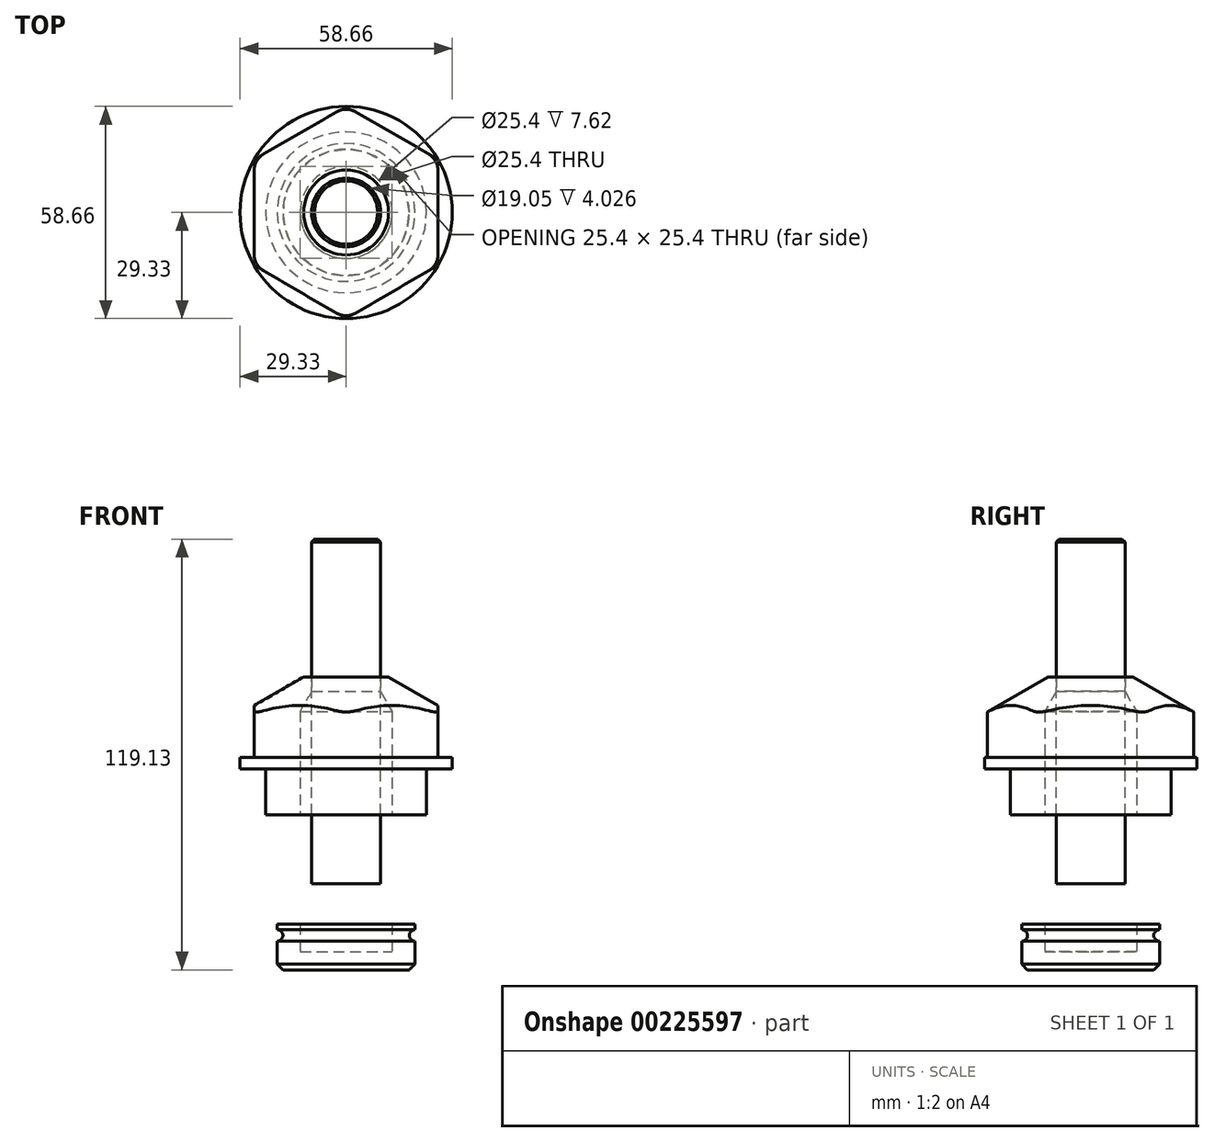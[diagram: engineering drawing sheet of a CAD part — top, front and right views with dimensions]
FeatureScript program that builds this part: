
annotation { "Feature Type Name" : "Feature", "Feature Type Description" : "" }
export const myFeature = defineFeature(function(context is Context, id is Id, definition is map)
    precondition{}
    {
        {
            var Q0;
            Q0=qCreatedBy(makeId("Top.planeOp"),FACE);
            var sketch = newSketch(context, id + "F0", { "sketchPlane" : qUnion([Q0])});
            skCircle(sketch, "E0", {"center": v(0, 0) * mm, "radius": 29.33 * mm});
            skLineSegment(sketch, "E1", {"start": v(0, 29.33) * mm, "end": v(0, -29.33) * mm, "construction": true});
            skLineSegment(sketch, "E2", {"start": v(-25.4, 14.66) * mm, "end": v(25.4, -14.66) * mm, "construction": true});
            skLineSegment(sketch, "E3", {"start": v(-25.4, -14.66) * mm, "end": v(25.4, 14.66) * mm, "construction": true});
            skLineSegment(sketch, "E4", {"start": v(-25.4, 14.66) * mm, "end": v(0, 29.33) * mm});
            skLineSegment(sketch, "E5", {"start": v(0, 29.33) * mm, "end": v(25.4, 14.66) * mm});
            skLineSegment(sketch, "E6", {"start": v(25.4, 14.66) * mm, "end": v(25.4, -14.66) * mm});
            skLineSegment(sketch, "E7", {"start": v(25.4, -14.66) * mm, "end": v(0, -29.33) * mm});
            skLineSegment(sketch, "E8", {"start": v(0, -29.33) * mm, "end": v(-25.4, -14.66) * mm});
            skLineSegment(sketch, "E9", {"start": v(-25.4, -14.66) * mm, "end": v(-25.4, 14.66) * mm});
            skCircle(sketch, "E10", {"center": v(0, 0) * mm, "radius": 7.94 * mm});
            skSolve(sketch);
        }
        {
            var Q0;
            Q0=makeQuery(id+"F0.imprint","IMPRINT",FACE,{"disambiguationData":[TD([[makeQuery(id+"F0.imprint","IMPRINT",EDGE,{"derivedFrom":sQuery(id+"F0.wireOp",EDGE,"E10")}),1.0]])]});
            var Q1;
            Q1=makeQuery(id+"F0.imprint","IMPRINT",FACE,{"disambiguationData":[TD([[makeQuery(id+"F0.imprint","IMPRINT",EDGE,{"derivedFrom":sQuery(id+"F0.wireOp",EDGE,"E4")}),-1.0]])]});
            extrude(context, id + "F1", {"entities" : qUnion([Q0, Q1]), "depth" : 25.4 * mm});
        }
        {
            var Q0;
            {var subQ0=sQuery(id+"F0.wireOp",EDGE,"E8");Q0=makeQuery(id+"F0.imprint","IMPRINT",FACE,{"disambiguationData":[TD([[makeQuery(id+"F0.imprint","IMPRINT",EDGE,{"derivedFrom":subQ0}),1.0]])]});}
            var Q1;
            {var subQ0=sQuery(id+"F0.wireOp",EDGE,"E7");Q1=makeQuery(id+"F0.imprint","IMPRINT",FACE,{"disambiguationData":[TD([[makeQuery(id+"F0.imprint","IMPRINT",EDGE,{"derivedFrom":subQ0}),1.0]])]});}
            var Q2;
            {var subQ0=sQuery(id+"F0.wireOp",EDGE,"E6");Q2=makeQuery(id+"F0.imprint","IMPRINT",FACE,{"disambiguationData":[TD([[makeQuery(id+"F0.imprint","IMPRINT",EDGE,{"derivedFrom":subQ0}),1.0]])]});}
            var Q3;
            Q3=makeQuery(id+"F0.imprint","IMPRINT",FACE,{"disambiguationData":[TD([[makeQuery(id+"F0.imprint","IMPRINT",EDGE,{"derivedFrom":sQuery(id+"F0.wireOp",EDGE,"E4")}),-1.0]])]});
            var Q4;
            {var subQ0=sQuery(id+"F0.wireOp",EDGE,"E5");Q4=makeQuery(id+"F0.imprint","IMPRINT",FACE,{"disambiguationData":[TD([[makeQuery(id+"F0.imprint","IMPRINT",EDGE,{"derivedFrom":subQ0}),1.0]])]});}
            var Q5;
            {var subQ0=sQuery(id+"F0.wireOp",EDGE,"E4");Q5=makeQuery(id+"F0.imprint","IMPRINT",FACE,{"disambiguationData":[TD([[makeQuery(id+"F0.imprint","IMPRINT",EDGE,{"derivedFrom":subQ0}),1.0]])]});}
            var Q6;
            {var subQ0=sQuery(id+"F0.wireOp",EDGE,"E9");Q6=makeQuery(id+"F0.imprint","IMPRINT",FACE,{"disambiguationData":[TD([[makeQuery(id+"F0.imprint","IMPRINT",EDGE,{"derivedFrom":subQ0}),1.0]])]});}
            extrude(context, id + "F2", {"entities" : qUnion([Q0, Q1, Q2, Q3, Q4, Q5, Q6]), "operationType" : NewBodyOperationType.ADD, "depth" : 3.17 * mm});
        }
        {
            var Q0;
            Q0=makeQuery(id+"F1.opExtrude","SWEPT_EDGE",EDGE,{"disambiguationData":[OSD([sQuery(id+"F0.wireOp",EDGE,"E0"),sQuery(id+"F0.wireOp",EDGE,"E7"),sQuery(id+"F0.wireOp",EDGE,"E8")])]});
            var Q1;
            Q1=makeQuery(id+"F1.opExtrude","SWEPT_EDGE",EDGE,{"disambiguationData":[OSD([sQuery(id+"F0.wireOp",EDGE,"E0"),sQuery(id+"F0.wireOp",EDGE,"E6"),sQuery(id+"F0.wireOp",EDGE,"E7")])]});
            var Q2;
            Q2=makeQuery(id+"F1.opExtrude","SWEPT_EDGE",EDGE,{"disambiguationData":[OSD([sQuery(id+"F0.wireOp",EDGE,"E0"),sQuery(id+"F0.wireOp",EDGE,"E5"),sQuery(id+"F0.wireOp",EDGE,"E6")])]});
            var Q3;
            Q3=makeQuery(id+"F1.opExtrude","SWEPT_EDGE",EDGE,{"disambiguationData":[OSD([sQuery(id+"F0.wireOp",EDGE,"E0"),sQuery(id+"F0.wireOp",EDGE,"E4"),sQuery(id+"F0.wireOp",EDGE,"E5")])]});
            var Q4;
            Q4=makeQuery(id+"F1.opExtrude","SWEPT_EDGE",EDGE,{"disambiguationData":[OSD([sQuery(id+"F0.wireOp",EDGE,"E0"),sQuery(id+"F0.wireOp",EDGE,"E4"),sQuery(id+"F0.wireOp",EDGE,"E9")])]});
            var Q5;
            Q5=makeQuery(id+"F1.opExtrude","SWEPT_EDGE",EDGE,{"disambiguationData":[OSD([sQuery(id+"F0.wireOp",EDGE,"E0"),sQuery(id+"F0.wireOp",EDGE,"E8"),sQuery(id+"F0.wireOp",EDGE,"E9")])]});
            fillet(context, id + "F3", {"entities" : qUnion([Q0, Q1, Q2, Q3, Q4, Q5]), "radius" : 5.08 * mm, "tangentPropagation" : true, "allowEdgeOverflow" : false});
        }
        {
            var Q0;
            Q0=qCreatedBy(makeId("Right.planeOp"),FACE);
            var sketch = newSketch(context, id + "F4", { "sketchPlane" : qUnion([Q0])});
            skLineSegment(sketch, "E11", {"start": v(0, 52) * mm, "end": v(0, 0) * mm, "construction": true});
            skLineSegment(sketch, "E12", {"start": v(11.73, 25.4) * mm, "end": v(35.4, 11.74) * mm});
            skLineSegment(sketch, "E13", {"start": v(35.4, 11.74) * mm, "end": v(35.4, 25.4) * mm});
            skLineSegment(sketch, "E14", {"start": v(35.4, 25.4) * mm, "end": v(11.73, 25.4) * mm});
            skLineSegment(sketch, "E15.0", {"start": v(11.73, 25.4) * mm, "end": v(-11.73, 25.4) * mm});
            skLineSegment(sketch, "E16.bottom", {"start": v(0, 0) * mm, "end": v(22.23, 0) * mm});
            skLineSegment(sketch, "E16.top", {"start": v(0, -12.7) * mm, "end": v(22.23, -12.7) * mm});
            skLineSegment(sketch, "E16.left", {"start": v(0, 0) * mm, "end": v(0, -12.7) * mm});
            skLineSegment(sketch, "E16.right", {"start": v(22.23, 0) * mm, "end": v(22.23, -12.7) * mm});
            skLineSegment(sketch, "E17.bottom", {"start": v(0, -12.7) * mm, "end": v(19.05, -12.7) * mm});
            skLineSegment(sketch, "E17.top", {"start": v(0, -27.69) * mm, "end": v(19.05, -27.69) * mm});
            skLineSegment(sketch, "E17.left", {"start": v(0, -12.7) * mm, "end": v(0, -27.69) * mm});
            skLineSegment(sketch, "E17.right", {"start": v(19.05, -12.7) * mm, "end": v(19.05, -27.69) * mm});
            skLineSegment(sketch, "E18.bottom", {"start": v(17.78, -27.69) * mm, "end": v(0, -27.69) * mm});
            skLineSegment(sketch, "E18.top", {"start": v(17.78, -42.93) * mm, "end": v(0, -42.93) * mm});
            skLineSegment(sketch, "E18.left", {"start": v(17.78, -27.69) * mm, "end": v(17.78, -42.93) * mm});
            skLineSegment(sketch, "E18.right", {"start": v(0, -27.69) * mm, "end": v(0, -42.93) * mm});
            skLineSegment(sketch, "E19.bottom", {"start": v(0, -42.93) * mm, "end": v(19.05, -42.93) * mm});
            skLineSegment(sketch, "E19.top", {"start": v(0, -55.63) * mm, "end": v(19.05, -55.63) * mm});
            skLineSegment(sketch, "E19.left", {"start": v(0, -42.93) * mm, "end": v(0, -55.63) * mm});
            skLineSegment(sketch, "E19.right", {"start": v(19.05, -42.93) * mm, "end": v(19.05, -55.63) * mm});
            skCircle(sketch, "E20", {"center": v(19.05, -24.51) * mm, "radius": 1.59 * mm});
            skCircle(sketch, "E21", {"center": v(19.05, -46.1) * mm, "radius": 1.59 * mm});
            skCircle(sketch, "E22", {"center": v(0, -17.46) * mm, "radius": 3.18 * mm});
            skCircle(sketch, "E23", {"center": v(0, -35.3) * mm, "radius": 3.18 * mm});
            skSolve(sketch);
        }
        {
            var Q0;
            Q0=makeQuery(id+"F4.imprint","IMPRINT",FACE,{"disambiguationData":[TD([[makeQuery(id+"F4.imprint","IMPRINT",EDGE,{"derivedFrom":sQuery(id+"F4.wireOp",EDGE,"E12")}),1.0]])]});
            var Q1;
            Q1=sQuery(id+"F4.wireOp",EDGE,"E11");
            revolve(context, id + "F5", {"operationType" : NewBodyOperationType.REMOVE, "entities" : qUnion([Q0]), "axis" : qUnion([Q1]), "revolveType" : RevolveType.FULL, "oppositeDirection" : true});
        }
        {
            var Q0;
            {var subQ7=sQuery(id+"F4.wireOp",EDGE,"E18.bottom");Q0=makeQuery(id+"F4.imprint","IMPRINT",FACE,{"disambiguationData":[TD([[makeQuery(id+"F4.imprint","IMPRINT",EDGE,{"derivedFrom":subQ7}),1.0]])]});}
            var Q1;
            {var subQ10=sQuery(id+"F4.wireOp",EDGE,"E17.bottom");Q1=makeQuery(id+"F4.imprint","IMPRINT",FACE,{"disambiguationData":[TD([[makeQuery(id+"F4.imprint","IMPRINT",EDGE,{"derivedFrom":subQ10}),-1.0]])]});}
            var Q2;
            Q2=makeQuery(id+"F4.imprint","IMPRINT",FACE,{"disambiguationData":[TD([[makeQuery(id+"F4.imprint","IMPRINT",EDGE,{"derivedFrom":sQuery(id+"F4.wireOp",EDGE,"E16.bottom")}),-1.0]])]});
            var Q3;
            {var subQ4=sQuery(id+"F4.wireOp",EDGE,"E19.top");Q3=makeQuery(id+"F4.imprint","IMPRINT",FACE,{"disambiguationData":[TD([[makeQuery(id+"F4.imprint","IMPRINT",EDGE,{"derivedFrom":subQ4}),1.0]])]});}
            var Q4;
            Q4=sQuery(id+"F4.wireOp",EDGE,"E11");
            revolve(context, id + "F6", {"operationType" : NewBodyOperationType.ADD, "entities" : qUnion([Q0, Q1, Q2, Q3]), "axis" : qUnion([Q4]), "revolveType" : RevolveType.FULL});
        }
        {
            var Q0;
            Q0=makeQuery(id+"F6.opRevolve","SWEPT_EDGE",EDGE,{"disambiguationData":[OSD([sQuery(id+"F4.wireOp",EDGE,"E19.top"),sQuery(id+"F4.wireOp",EDGE,"E19.right")])]});
            chamfer(context, id + "F7", {"entities" : qUnion([Q0]), "width" : 1.59 * mm, "tangentPropagation" : true});
        }
        {
            var Q0;
            {var subQ0=sQuery(id+"F4.wireOp",EDGE,"E16.right");var subQ1=sQuery(id+"F4.wireOp",EDGE,"E20");var subQ3=makeQuery(id+"F4.imprint","INTERSECT",VERTEX,{"disambiguationData":[OD(0.0)],"derivedFrom":[subQ0,subQ1]});Q0=makeQuery(id+"F4.imprint","IMPRINT",FACE,{"disambiguationData":[TD([[makeQuery(id+"F4.imprint","SKETCH_ENTITY",EDGE,{"disambiguationData":[TD([[subQ3,-1.0]])],"sketchEntityId":"E16.right"}),1.0]])]});}
            var Q1;
            {var subQ0=sQuery(id+"F4.wireOp",EDGE,"E20");var subQ1=sQuery(id+"F4.wireOp",EDGE,"E17.right");var subQ3=makeQuery(id+"F4.imprint","INTERSECT",VERTEX,{"disambiguationData":[OD(0.0)],"derivedFrom":[subQ1,subQ0]});Q1=makeQuery(id+"F4.imprint","IMPRINT",FACE,{"disambiguationData":[TD([[makeQuery(id+"F4.imprint","IMPRINT",EDGE,{"disambiguationData":[TD([[subQ3,-1.0]])],"derivedFrom":subQ1}),-1.0]])]});}
            var Q2;
            {var subQ0=sQuery(id+"F4.wireOp",EDGE,"E20");var subQ1=sQuery(id+"F4.wireOp",EDGE,"E17.right");var subQ3=makeQuery(id+"F4.imprint","INTERSECT",VERTEX,{"disambiguationData":[OD(0.0)],"derivedFrom":[subQ1,subQ0]});Q2=makeQuery(id+"F4.imprint","IMPRINT",FACE,{"disambiguationData":[TD([[makeQuery(id+"F4.imprint","IMPRINT",EDGE,{"disambiguationData":[TD([[subQ3,-1.0]])],"derivedFrom":subQ1}),1.0]])]});}
            var Q3;
            Q3=sQuery(id+"F4.wireOp",EDGE,"E11");
            revolve(context, id + "F8", {"entities" : qUnion([Q0, Q1, Q2]), "axis" : qUnion([Q3]), "revolveType" : RevolveType.FULL});
        }
        {
            var Q0;
            {var subQ0=sQuery(id+"F4.wireOp",EDGE,"E22");var subQ1=sQuery(id+"F4.wireOp",EDGE,"E17.left");var subQ3=makeQuery(id+"F4.imprint","INTERSECT",VERTEX,{"disambiguationData":[OD(0.0)],"derivedFrom":[subQ1,subQ0]});Q0=makeQuery(id+"F4.imprint","IMPRINT",FACE,{"disambiguationData":[TD([[makeQuery(id+"F4.imprint","IMPRINT",EDGE,{"disambiguationData":[TD([[subQ3,-1.0]])],"derivedFrom":subQ1}),-1.0]])]});}
            var Q1;
            {var subQ0=sQuery(id+"F4.wireOp",EDGE,"E22");var subQ1=sQuery(id+"F4.wireOp",EDGE,"E17.left");var subQ3=makeQuery(id+"F4.imprint","INTERSECT",VERTEX,{"disambiguationData":[OD(0.0)],"derivedFrom":[subQ1,subQ0]});Q1=makeQuery(id+"F4.imprint","IMPRINT",FACE,{"disambiguationData":[TD([[makeQuery(id+"F4.imprint","IMPRINT",EDGE,{"disambiguationData":[TD([[subQ3,-1.0]])],"derivedFrom":subQ1}),1.0]])]});}
            var Q2;
            {var subQ0=sQuery(id+"F4.wireOp",EDGE,"E23");var subQ1=sQuery(id+"F4.wireOp",EDGE,"E18.right");var subQ3=makeQuery(id+"F4.imprint","INTERSECT",VERTEX,{"disambiguationData":[OD(0.0)],"derivedFrom":[subQ1,subQ0]});Q2=makeQuery(id+"F4.imprint","IMPRINT",FACE,{"disambiguationData":[TD([[makeQuery(id+"F4.imprint","IMPRINT",EDGE,{"disambiguationData":[TD([[subQ3,-1.0]])],"derivedFrom":subQ1}),-1.0]])]});}
            var Q3;
            {var subQ0=sQuery(id+"F4.wireOp",EDGE,"E23");var subQ1=sQuery(id+"F4.wireOp",EDGE,"E18.right");var subQ3=makeQuery(id+"F4.imprint","INTERSECT",VERTEX,{"disambiguationData":[OD(0.0)],"derivedFrom":[subQ1,subQ0]});Q3=makeQuery(id+"F4.imprint","IMPRINT",FACE,{"disambiguationData":[TD([[makeQuery(id+"F4.imprint","IMPRINT",EDGE,{"disambiguationData":[TD([[subQ3,-1.0]])],"derivedFrom":subQ1}),1.0]])]});}
            extrude(context, id + "F9", {"entities" : qUnion([Q0, Q1, Q2, Q3]), "operationType" : NewBodyOperationType.REMOVE, "endBound" : BoundingType.THROUGH_ALL, "depth" : 25.4 * mm});
        }
        {
            var Q0;
            Q0=qCreatedBy(makeId("Right.planeOp"),FACE);
            var sketch = newSketch(context, id + "F10", { "sketchPlane" : qUnion([Q0])});
            skLineSegment(sketch, "E24", {"start": v(0, 63.5) * mm, "end": v(0, -50.55) * mm});
            skLineSegment(sketch, "E25", {"start": v(0, -50.55) * mm, "end": v(12.7, -50.55) * mm});
            skLineSegment(sketch, "E26", {"start": v(12.7, -50.55) * mm, "end": v(12.7, 15.88) * mm});
            skLineSegment(sketch, "E27", {"start": v(12.7, 15.88) * mm, "end": v(0, 15.88) * mm});
            skLineSegment(sketch, "E28", {"start": v(9.53, -31.75) * mm, "end": v(9.53, 63.5) * mm});
            skLineSegment(sketch, "E29", {"start": v(9.52, 63.5) * mm, "end": v(0, 63.5) * mm});
            skLineSegment(sketch, "E30", {"start": v(9.53, 21.37) * mm, "end": v(12.7, 15.88) * mm});
            skLineSegment(sketch, "E31.rect.bottom", {"start": v(12.7, -38.1) * mm, "end": v(-12.7, -38.1) * mm});
            skLineSegment(sketch, "E31.rect.top", {"start": v(12.7, -31.75) * mm, "end": v(-12.7, -31.75) * mm});
            skLineSegment(sketch, "E31.rect.left", {"start": v(12.7, -38.1) * mm, "end": v(12.7, -31.75) * mm});
            skLineSegment(sketch, "E31.rect.right", {"start": v(-12.7, -38.1) * mm, "end": v(-12.7, -31.75) * mm});
            skPoint(sketch, "E31.rect.middle", {"position": v(0, -34.92) * mm});
            skSolve(sketch);
        }
        {
            var Q0;
            {var subQ0=sQuery(id+"F10.wireOp",EDGE,"E29");Q0=makeQuery(id+"F10.imprint","IMPRINT",FACE,{"disambiguationData":[TD([[makeQuery(id+"F10.imprint","IMPRINT",EDGE,{"derivedFrom":subQ0}),1.0]])]});}
            var Q1;
            {var subQ0=sQuery(id+"F10.wireOp",EDGE,"E30");Q1=makeQuery(id+"F10.imprint","IMPRINT",FACE,{"disambiguationData":[TD([[makeQuery(id+"F10.imprint","IMPRINT",EDGE,{"derivedFrom":subQ0}),-1.0]])]});}
            var Q2;
            {var subQ1=sQuery(id+"F10.wireOp",EDGE,"E24");var subQ5=sQuery(id+"F10.wireOp",EDGE,"E27");var subQ7=makeQuery(id+"F10.imprint","INTERSECT",VERTEX,{"derivedFrom":[subQ1,subQ5]});Q2=makeQuery(id+"F10.imprint","IMPRINT",FACE,{"disambiguationData":[TD([[makeQuery(id+"F10.imprint","IMPRINT",EDGE,{"disambiguationData":[TD([[subQ7,-1.0]])],"derivedFrom":subQ1}),1.0]])]});}
            var Q3;
            {var subQ0=sQuery(id+"F10.wireOp",EDGE,"E31.rect.top");var subQ3=sQuery(id+"F10.wireOp",EDGE,"E28");var subQ4=makeQuery(id+"F10.imprint","INTERSECT",VERTEX,{"derivedFrom":[subQ3,subQ0]});Q3=makeQuery(id+"F10.imprint","IMPRINT",FACE,{"disambiguationData":[TD([[makeQuery(id+"F10.imprint","IMPRINT",EDGE,{"disambiguationData":[TD([[subQ4,-1.0]])],"derivedFrom":subQ3}),-1.0]])]});}
            var Q4;
            {var subQ5=sQuery(id+"F10.wireOp",EDGE,"E25");Q4=makeQuery(id+"F10.imprint","IMPRINT",FACE,{"disambiguationData":[TD([[makeQuery(id+"F10.imprint","IMPRINT",EDGE,{"derivedFrom":subQ5}),1.0]])]});}
            var Q5;
            {var subQ0=sQuery(id+"F10.wireOp",EDGE,"E31.rect.left");Q5=makeQuery(id+"F10.imprint","IMPRINT",FACE,{"disambiguationData":[TD([[makeQuery(id+"F10.imprint","IMPRINT",EDGE,{"derivedFrom":subQ0}),1.0]])]});}
            var Q6;
            Q6=sQuery(id+"F10.wireOp",EDGE,"E24");
            revolve(context, id + "F11", {"operationType" : NewBodyOperationType.REMOVE, "entities" : qUnion([Q0, Q1, Q2, Q3, Q4, Q5]), "axis" : qUnion([Q6]), "revolveType" : RevolveType.FULL, "oppositeDirection" : true});
        }
        {
            var Q0;
            {var subQ0=sQuery(id+"F10.wireOp",EDGE,"E29");Q0=makeQuery(id+"F10.imprint","IMPRINT",FACE,{"disambiguationData":[TD([[makeQuery(id+"F10.imprint","IMPRINT",EDGE,{"derivedFrom":subQ0}),1.0]])]});}
            var Q1;
            {var subQ1=sQuery(id+"F10.wireOp",EDGE,"E24");var subQ5=sQuery(id+"F10.wireOp",EDGE,"E27");var subQ7=makeQuery(id+"F10.imprint","INTERSECT",VERTEX,{"derivedFrom":[subQ1,subQ5]});Q1=makeQuery(id+"F10.imprint","IMPRINT",FACE,{"disambiguationData":[TD([[makeQuery(id+"F10.imprint","IMPRINT",EDGE,{"disambiguationData":[TD([[subQ7,-1.0]])],"derivedFrom":subQ1}),1.0]])]});}
            var Q2;
            {var subQ0=sQuery(id+"F10.wireOp",EDGE,"E31.rect.left");Q2=makeQuery(id+"F10.imprint","IMPRINT",FACE,{"disambiguationData":[TD([[makeQuery(id+"F10.imprint","IMPRINT",EDGE,{"derivedFrom":subQ0}),1.0]])]});}
            var Q3;
            Q3=sQuery(id+"F10.wireOp",EDGE,"E24");
            revolve(context, id + "F12", {"entities" : qUnion([Q0, Q1, Q2]), "axis" : qUnion([Q3]), "revolveType" : RevolveType.FULL});
        }
        {
            var Q0;
            Q0=makeQuery(id+"F12.opRevolve","SWEPT_FACE",FACE,{"disambiguationData":[OSD([sQuery(id+"F10.wireOp",EDGE,"E29")])]});
            chamfer(context, id + "F13", {"entities" : qUnion([Q0]), "width" : 0.8 * mm, "tangentPropagation" : true});
        }
    });
